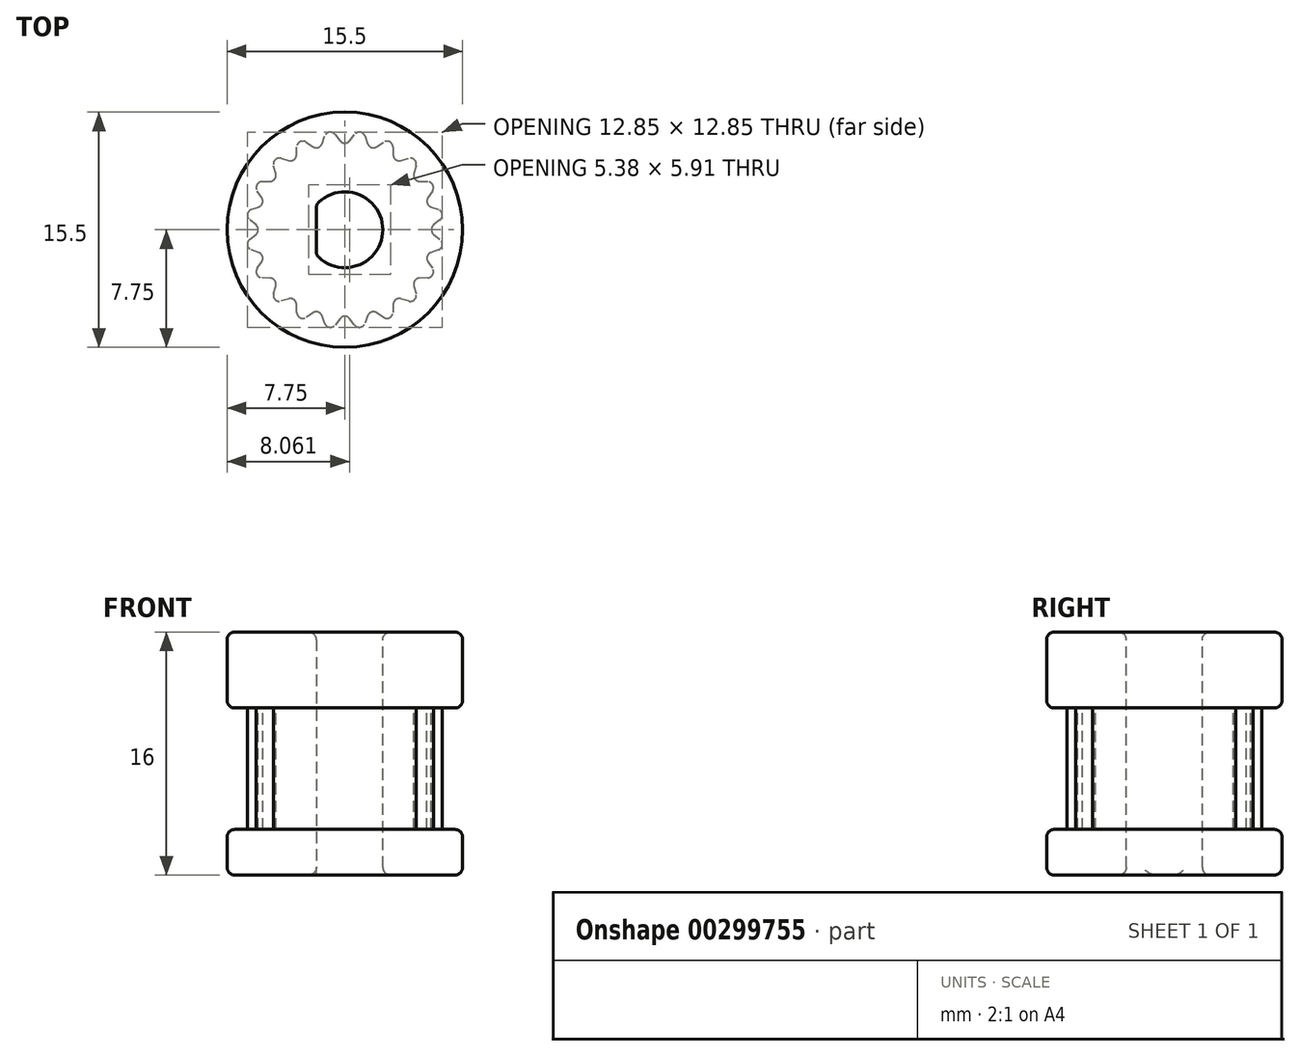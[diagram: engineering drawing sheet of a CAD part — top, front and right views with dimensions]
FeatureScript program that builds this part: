
annotation { "Feature Type Name" : "Feature", "Feature Type Description" : "" }
export const myFeature = defineFeature(function(context is Context, id is Id, definition is map)
    precondition{}
    {
        {
            var Q0;
            Q0=qCreatedBy(makeId("Top.planeOp"),FACE);
            var sketch = newSketch(context, id + "F0", { "sketchPlane" : qUnion([Q0])});
            skCircle(sketch, "E0", {"center": v(0, 0) * mm, "radius": 7.75 * mm});
            skCircle(sketch, "E1.cCircle", {"center": v(0, 0) * mm, "radius": 6.5 * mm, "construction": true});
            skCircle(sketch, "E2", {"center": v(0, 0) * mm, "radius": 5.7 * mm, "construction": true});
            skArc(sketch, "E3.filletArc", {"start": v(1.33, 6.16) * mm, "mid": v(1.02, 6.42) * mm, "end": v(0.64, 6.27) * mm});
            skArc(sketch, "E4.filletArc", {"start": v(-0.32, 5.85) * mm, "mid": v(0, 5.7) * mm, "end": v(0.32, 5.85) * mm});
            skArc(sketch, "E5.filletArc", {"start": v(-0.64, 6.27) * mm, "mid": v(-0.8, 6.4) * mm, "end": v(-1.02, 6.42) * mm, "construction": true});
            skLineSegment(sketch, "E6", {"start": v(0, 0) * mm, "end": v(-0.95, 6.02) * mm, "construction": true});
            skLineSegment(sketch, "E7", {"start": v(0, 0) * mm, "end": v(0.95, 6.02) * mm, "construction": true});
            skLineSegment(sketch, "E8", {"start": v(0, 0) * mm, "end": v(0, 6.1) * mm, "construction": true});
            skLineSegment(sketch, "E9", {"start": v(-0.64, 6.27) * mm, "end": v(-0.32, 5.85) * mm});
            skLineSegment(sketch, "E10", {"start": v(0.32, 5.85) * mm, "end": v(0.64, 6.27) * mm});
            skLineSegment(sketch, "E11.1.0", {"start": v(-2.54, 5.77) * mm, "end": v(-2.1, 5.47) * mm});
            skArc(sketch, "E11.1.1", {"start": v(-2.1, 5.47) * mm, "mid": v(-1.76, 5.42) * mm, "end": v(-1.5, 5.67) * mm});
            skLineSegment(sketch, "E11.1.2", {"start": v(-1.5, 5.67) * mm, "end": v(-1.33, 6.16) * mm});
            skArc(sketch, "E11.1.3", {"start": v(-0.64, 6.27) * mm, "mid": v(-1.02, 6.42) * mm, "end": v(-1.33, 6.16) * mm});
            skLineSegment(sketch, "E11.2.0", {"start": v(-4.2, 4.7) * mm, "end": v(-3.7, 4.55) * mm});
            skArc(sketch, "E11.2.1", {"start": v(-3.7, 4.55) * mm, "mid": v(-3.35, 4.61) * mm, "end": v(-3.19, 4.92) * mm});
            skLineSegment(sketch, "E11.2.2", {"start": v(-3.19, 4.92) * mm, "end": v(-3.17, 5.45) * mm});
            skArc(sketch, "E11.2.3", {"start": v(-2.54, 5.77) * mm, "mid": v(-2.95, 5.8) * mm, "end": v(-3.17, 5.45) * mm});
            skLineSegment(sketch, "E11.3.0", {"start": v(-5.45, 3.17) * mm, "end": v(-4.92, 3.19) * mm});
            skArc(sketch, "E11.3.1", {"start": v(-4.92, 3.19) * mm, "mid": v(-4.61, 3.35) * mm, "end": v(-4.55, 3.7) * mm});
            skLineSegment(sketch, "E11.3.2", {"start": v(-4.55, 3.7) * mm, "end": v(-4.7, 4.2) * mm});
            skArc(sketch, "E11.3.3", {"start": v(-4.2, 4.7) * mm, "mid": v(-4.6, 4.6) * mm, "end": v(-4.7, 4.2) * mm});
            skLineSegment(sketch, "E11.4.0", {"start": v(-6.16, 1.33) * mm, "end": v(-5.67, 1.5) * mm});
            skArc(sketch, "E11.4.1", {"start": v(-5.67, 1.5) * mm, "mid": v(-5.42, 1.76) * mm, "end": v(-5.47, 2.1) * mm});
            skLineSegment(sketch, "E11.4.2", {"start": v(-5.47, 2.1) * mm, "end": v(-5.77, 2.54) * mm});
            skArc(sketch, "E11.4.3", {"start": v(-5.45, 3.17) * mm, "mid": v(-5.8, 2.95) * mm, "end": v(-5.77, 2.54) * mm});
            skLineSegment(sketch, "E11.5.0", {"start": v(-6.27, -0.64) * mm, "end": v(-5.85, -0.32) * mm});
            skArc(sketch, "E11.5.1", {"start": v(-5.85, -0.32) * mm, "mid": v(-5.7, 0) * mm, "end": v(-5.85, 0.32) * mm});
            skLineSegment(sketch, "E11.5.2", {"start": v(-5.85, 0.32) * mm, "end": v(-6.27, 0.64) * mm});
            skArc(sketch, "E11.5.3", {"start": v(-6.16, 1.33) * mm, "mid": v(-6.42, 1.02) * mm, "end": v(-6.27, 0.64) * mm});
            skLineSegment(sketch, "E11.6.0", {"start": v(-5.77, -2.54) * mm, "end": v(-5.47, -2.1) * mm});
            skArc(sketch, "E11.6.1", {"start": v(-5.47, -2.1) * mm, "mid": v(-5.42, -1.76) * mm, "end": v(-5.67, -1.5) * mm});
            skLineSegment(sketch, "E11.6.2", {"start": v(-5.67, -1.5) * mm, "end": v(-6.16, -1.33) * mm});
            skArc(sketch, "E11.6.3", {"start": v(-6.27, -0.64) * mm, "mid": v(-6.42, -1.02) * mm, "end": v(-6.16, -1.33) * mm});
            skLineSegment(sketch, "E11.7.0", {"start": v(-4.7, -4.2) * mm, "end": v(-4.55, -3.7) * mm});
            skArc(sketch, "E11.7.1", {"start": v(-4.55, -3.7) * mm, "mid": v(-4.61, -3.35) * mm, "end": v(-4.92, -3.19) * mm});
            skLineSegment(sketch, "E11.7.2", {"start": v(-4.92, -3.19) * mm, "end": v(-5.45, -3.17) * mm});
            skArc(sketch, "E11.7.3", {"start": v(-5.77, -2.54) * mm, "mid": v(-5.8, -2.95) * mm, "end": v(-5.45, -3.17) * mm});
            skLineSegment(sketch, "E11.8.0", {"start": v(-3.17, -5.45) * mm, "end": v(-3.19, -4.92) * mm});
            skArc(sketch, "E11.8.1", {"start": v(-3.19, -4.92) * mm, "mid": v(-3.35, -4.61) * mm, "end": v(-3.7, -4.55) * mm});
            skLineSegment(sketch, "E11.8.2", {"start": v(-3.7, -4.55) * mm, "end": v(-4.2, -4.7) * mm});
            skArc(sketch, "E11.8.3", {"start": v(-4.7, -4.2) * mm, "mid": v(-4.6, -4.6) * mm, "end": v(-4.2, -4.7) * mm});
            skLineSegment(sketch, "E11.9.0", {"start": v(-1.33, -6.16) * mm, "end": v(-1.5, -5.67) * mm});
            skArc(sketch, "E11.9.1", {"start": v(-1.5, -5.67) * mm, "mid": v(-1.76, -5.42) * mm, "end": v(-2.1, -5.47) * mm});
            skLineSegment(sketch, "E11.9.2", {"start": v(-2.1, -5.47) * mm, "end": v(-2.54, -5.77) * mm});
            skArc(sketch, "E11.9.3", {"start": v(-3.17, -5.45) * mm, "mid": v(-2.95, -5.8) * mm, "end": v(-2.54, -5.77) * mm});
            skLineSegment(sketch, "E11.10.0", {"start": v(0.64, -6.27) * mm, "end": v(0.32, -5.85) * mm});
            skArc(sketch, "E11.10.1", {"start": v(0.32, -5.85) * mm, "mid": v(0, -5.7) * mm, "end": v(-0.32, -5.85) * mm});
            skLineSegment(sketch, "E11.10.2", {"start": v(-0.32, -5.85) * mm, "end": v(-0.64, -6.27) * mm});
            skArc(sketch, "E11.10.3", {"start": v(-1.33, -6.16) * mm, "mid": v(-1.02, -6.42) * mm, "end": v(-0.64, -6.27) * mm});
            skLineSegment(sketch, "E11.11.0", {"start": v(2.54, -5.77) * mm, "end": v(2.1, -5.47) * mm});
            skArc(sketch, "E11.11.1", {"start": v(2.1, -5.47) * mm, "mid": v(1.76, -5.42) * mm, "end": v(1.5, -5.67) * mm});
            skLineSegment(sketch, "E11.11.2", {"start": v(1.5, -5.67) * mm, "end": v(1.33, -6.16) * mm});
            skArc(sketch, "E11.11.3", {"start": v(0.64, -6.27) * mm, "mid": v(1.02, -6.42) * mm, "end": v(1.33, -6.16) * mm});
            skLineSegment(sketch, "E11.12.0", {"start": v(4.2, -4.7) * mm, "end": v(3.7, -4.55) * mm});
            skArc(sketch, "E11.12.1", {"start": v(3.7, -4.55) * mm, "mid": v(3.35, -4.61) * mm, "end": v(3.19, -4.92) * mm});
            skLineSegment(sketch, "E11.12.2", {"start": v(3.19, -4.92) * mm, "end": v(3.17, -5.45) * mm});
            skArc(sketch, "E11.12.3", {"start": v(2.54, -5.77) * mm, "mid": v(2.95, -5.8) * mm, "end": v(3.17, -5.45) * mm});
            skLineSegment(sketch, "E11.13.0", {"start": v(5.45, -3.17) * mm, "end": v(4.92, -3.19) * mm});
            skArc(sketch, "E11.13.1", {"start": v(4.92, -3.19) * mm, "mid": v(4.61, -3.35) * mm, "end": v(4.55, -3.7) * mm});
            skLineSegment(sketch, "E11.13.2", {"start": v(4.55, -3.7) * mm, "end": v(4.7, -4.2) * mm});
            skArc(sketch, "E11.13.3", {"start": v(4.2, -4.7) * mm, "mid": v(4.6, -4.6) * mm, "end": v(4.7, -4.2) * mm});
            skLineSegment(sketch, "E11.14.0", {"start": v(6.16, -1.33) * mm, "end": v(5.67, -1.5) * mm});
            skArc(sketch, "E11.14.1", {"start": v(5.67, -1.5) * mm, "mid": v(5.42, -1.76) * mm, "end": v(5.47, -2.1) * mm});
            skLineSegment(sketch, "E11.14.2", {"start": v(5.47, -2.1) * mm, "end": v(5.77, -2.54) * mm});
            skArc(sketch, "E11.14.3", {"start": v(5.45, -3.17) * mm, "mid": v(5.8, -2.95) * mm, "end": v(5.77, -2.54) * mm});
            skLineSegment(sketch, "E11.15.0", {"start": v(6.27, 0.64) * mm, "end": v(5.85, 0.32) * mm});
            skArc(sketch, "E11.15.1", {"start": v(5.85, 0.32) * mm, "mid": v(5.7, 0) * mm, "end": v(5.85, -0.32) * mm});
            skLineSegment(sketch, "E11.15.2", {"start": v(5.85, -0.32) * mm, "end": v(6.27, -0.64) * mm});
            skArc(sketch, "E11.15.3", {"start": v(6.16, -1.33) * mm, "mid": v(6.42, -1.02) * mm, "end": v(6.27, -0.64) * mm});
            skLineSegment(sketch, "E11.16.0", {"start": v(5.77, 2.54) * mm, "end": v(5.47, 2.1) * mm});
            skArc(sketch, "E11.16.1", {"start": v(5.47, 2.1) * mm, "mid": v(5.42, 1.76) * mm, "end": v(5.67, 1.5) * mm});
            skLineSegment(sketch, "E11.16.2", {"start": v(5.67, 1.5) * mm, "end": v(6.16, 1.33) * mm});
            skArc(sketch, "E11.16.3", {"start": v(6.27, 0.64) * mm, "mid": v(6.42, 1.02) * mm, "end": v(6.16, 1.33) * mm});
            skLineSegment(sketch, "E11.17.0", {"start": v(4.7, 4.2) * mm, "end": v(4.55, 3.7) * mm});
            skArc(sketch, "E11.17.1", {"start": v(4.55, 3.7) * mm, "mid": v(4.61, 3.35) * mm, "end": v(4.92, 3.19) * mm});
            skLineSegment(sketch, "E11.17.2", {"start": v(4.92, 3.19) * mm, "end": v(5.45, 3.17) * mm});
            skArc(sketch, "E11.17.3", {"start": v(5.77, 2.54) * mm, "mid": v(5.8, 2.95) * mm, "end": v(5.45, 3.17) * mm});
            skLineSegment(sketch, "E11.18.0", {"start": v(3.17, 5.45) * mm, "end": v(3.19, 4.92) * mm});
            skArc(sketch, "E11.18.1", {"start": v(3.19, 4.92) * mm, "mid": v(3.35, 4.61) * mm, "end": v(3.7, 4.55) * mm});
            skLineSegment(sketch, "E11.18.2", {"start": v(3.7, 4.55) * mm, "end": v(4.2, 4.7) * mm});
            skArc(sketch, "E11.18.3", {"start": v(4.7, 4.2) * mm, "mid": v(4.6, 4.6) * mm, "end": v(4.2, 4.7) * mm});
            skLineSegment(sketch, "E11.19.0", {"start": v(1.33, 6.16) * mm, "end": v(1.5, 5.67) * mm});
            skArc(sketch, "E11.19.1", {"start": v(1.5, 5.67) * mm, "mid": v(1.76, 5.42) * mm, "end": v(2.1, 5.47) * mm});
            skLineSegment(sketch, "E11.19.2", {"start": v(2.1, 5.47) * mm, "end": v(2.54, 5.77) * mm});
            skArc(sketch, "E11.19.3", {"start": v(3.17, 5.45) * mm, "mid": v(2.95, 5.8) * mm, "end": v(2.54, 5.77) * mm});
            skArc(sketch, "E12", {"start": v(-1.88, -1.65) * mm, "mid": v(2.5, 0) * mm, "end": v(-1.88, 1.65) * mm});
            skLineSegment(sketch, "E13", {"start": v(-1.88, 1.65) * mm, "end": v(-1.88, -1.65) * mm});
            skSolve(sketch);
        }
        {
            var Q0;
            Q0=makeQuery(id+"F0.imprint","IMPRINT",FACE,{"disambiguationData":[TD([[makeQuery(id+"F0.imprint","IMPRINT",EDGE,{"derivedFrom":sQuery(id+"F0.wireOp",EDGE,"E3.filletArc")}),1.0]])]});
            var Q1;
            Q1=makeQuery(id+"F0.imprint","IMPRINT",FACE,{"disambiguationData":[TD([[makeQuery(id+"F0.imprint","IMPRINT",EDGE,{"derivedFrom":sQuery(id+"F0.wireOp",EDGE,"E0")}),1.0]])]});
            extrude(context, id + "F1", {"entities" : qUnion([Q0, Q1]), "oppositeDirection" : true, "depth" : 5 * mm});
        }
        {
            var Q0;
            Q0=makeQuery(id+"F0.imprint","IMPRINT",FACE,{"disambiguationData":[TD([[makeQuery(id+"F0.imprint","IMPRINT",EDGE,{"derivedFrom":sQuery(id+"F0.wireOp",EDGE,"E3.filletArc")}),1.0]])]});
            extrude(context, id + "F2", {"entities" : qUnion([Q0]), "operationType" : NewBodyOperationType.ADD, "oppositeDirection" : true, "depth" : (8 + 5) * mm});
        }
        {
            var Q0;
            Q0=makeQuery(id+"F0.imprint","IMPRINT",FACE,{"disambiguationData":[TD([[makeQuery(id+"F0.imprint","IMPRINT",EDGE,{"derivedFrom":sQuery(id+"F0.wireOp",EDGE,"E0")}),1.0]])]});
            var Q1;
            Q1=makeQuery(id+"F0.imprint","IMPRINT",FACE,{"disambiguationData":[TD([[makeQuery(id+"F0.imprint","IMPRINT",EDGE,{"derivedFrom":sQuery(id+"F0.wireOp",EDGE,"E3.filletArc")}),1.0]])]});
            extrude(context, id + "F3", {"entities" : qUnion([Q0, Q1]), "operationType" : NewBodyOperationType.ADD, "oppositeDirection" : true, "depth" : (8 + 5 + 3) * mm, "hasSecondDirection" : true, "secondDirectionOppositeDirection" : true, "secondDirectionDepth" : (8 + 5) * mm});
        }
        {
            var Q0;
            Q0=makeQuery(id+"F1.opExtrude","CAP_EDGE",EDGE,{"disambiguationData":[OSD([sQuery(id+"F0.wireOp",EDGE,"E0")])],"isStart":true});
            var Q1;
            Q1=makeQuery(id+"F1.opExtrude","CAP_EDGE",EDGE,{"disambiguationData":[OSD([sQuery(id+"F0.wireOp",EDGE,"E0")])],"isStart":false});
            var Q2;
            Q2=makeQuery(id+"F3.opExtrude","CAP_EDGE",EDGE,{"disambiguationData":[OSD([sQuery(id+"F0.wireOp",EDGE,"E0")])],"isStart":true});
            var Q3;
            Q3=makeQuery(id+"F3.opExtrude","CAP_EDGE",EDGE,{"disambiguationData":[OSD([sQuery(id+"F0.wireOp",EDGE,"E0")])],"isStart":false});
            var Q4;
            Q4=makeQuery(id+"F1.opExtrude","CAP_EDGE",EDGE,{"disambiguationData":[OSD([sQuery(id+"F0.wireOp",EDGE,"E12")])],"isStart":true});
            var Q5;
            Q5=makeQuery(id+"F1.opExtrude","CAP_EDGE",EDGE,{"disambiguationData":[OSD([sQuery(id+"F0.wireOp",EDGE,"E13")])],"isStart":true});
            var Q6;
            {var subQ0=sQuery(id+"F0.wireOp",EDGE,"E13");var subQ1=sQuery(id+"F0.wireOp",EDGE,"E12");var subQ2=makeQuery(id+"F0.imprint","INTERSECT",VERTEX,{"disambiguationData":[OD(1.0)],"derivedFrom":[subQ1,subQ0]});Q6=makeQuery(id+"F3.boolean.opBoolean","MERGE",EDGE,{"derivedFrom":[makeQuery(id+"F2.boolean.opBoolean","MERGE",EDGE,{"derivedFrom":[makeQuery(id+"F1.opExtrude","SWEPT_EDGE",EDGE,{"disambiguationData":[OSD([subQ1,subQ0]),TDD([subQ2])]}),makeQuery(id+"F2.opExtrude","SWEPT_EDGE",EDGE,{"disambiguationData":[OSD([subQ1,subQ0]),TDD([subQ2])]})]}),makeQuery(id+"F3.opExtrude","SWEPT_EDGE",EDGE,{"disambiguationData":[OSD([subQ1,subQ0]),TDD([subQ2])]})]});}
            var Q7;
            {var subQ0=sQuery(id+"F0.wireOp",EDGE,"E13");var subQ1=sQuery(id+"F0.wireOp",EDGE,"E12");var subQ2=makeQuery(id+"F0.imprint","INTERSECT",VERTEX,{"disambiguationData":[OD(0.0)],"derivedFrom":[subQ1,subQ0]});Q7=makeQuery(id+"F3.boolean.opBoolean","MERGE",EDGE,{"derivedFrom":[makeQuery(id+"F2.boolean.opBoolean","MERGE",EDGE,{"derivedFrom":[makeQuery(id+"F1.opExtrude","SWEPT_EDGE",EDGE,{"disambiguationData":[OSD([subQ1,subQ0]),TDD([subQ2])]}),makeQuery(id+"F2.opExtrude","SWEPT_EDGE",EDGE,{"disambiguationData":[OSD([subQ1,subQ0]),TDD([subQ2])]})]}),makeQuery(id+"F3.opExtrude","SWEPT_EDGE",EDGE,{"disambiguationData":[OSD([subQ1,subQ0]),TDD([subQ2])]})]});}
            var Q8;
            Q8=makeQuery(id+"F3.opExtrude","CAP_EDGE",EDGE,{"disambiguationData":[OSD([sQuery(id+"F0.wireOp",EDGE,"E12")])],"isStart":false});
            fillet(context, id + "F4", {"entities" : qUnion([Q0, Q1, Q2, Q3, Q4, Q5, Q6, Q7, Q8]), "radius" : 0.5 * mm, "tangentPropagation" : true, "allowEdgeOverflow" : false});
        }
    });
